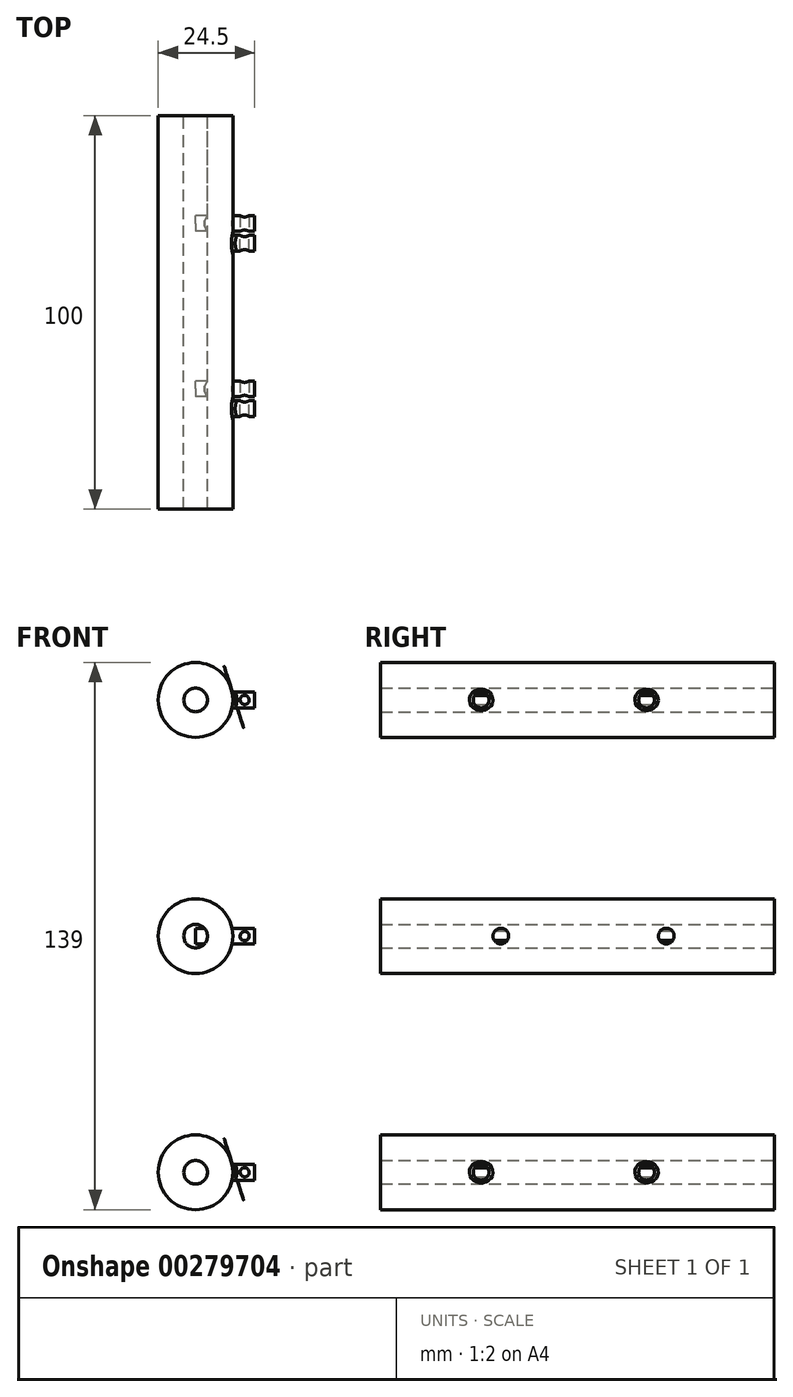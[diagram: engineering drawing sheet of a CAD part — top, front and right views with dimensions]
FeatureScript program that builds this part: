
annotation { "Feature Type Name" : "Feature", "Feature Type Description" : "" }
export const myFeature = defineFeature(function(context is Context, id is Id, definition is map)
    precondition{}
    {
        {
            var Q0;
            Q0=qCreatedBy(makeId("Front.planeOp"),FACE);
            var sketch = newSketch(context, id + "F0", { "sketchPlane" : qUnion([Q0])});
            skCircle(sketch, "E0", {"center": v(0, 0) * mm, "radius": 9.5 * mm});
            skCircle(sketch, "E1", {"center": v(0, 0) * mm, "radius": 3 * mm});
            skSolve(sketch);
        }
        {
            var Q0;
            Q0=makeQuery(id+"F0.imprint","IMPRINT",FACE,{"disambiguationData":[TD([[makeQuery(id+"F0.imprint","IMPRINT",EDGE,{"derivedFrom":sQuery(id+"F0.wireOp",EDGE,"E0")}),1.0]])]});
            extrude(context, id + "F1", {"entities" : qUnion([Q0]), "endBound" : BoundingType.SYMMETRIC, "depth" : 100 * mm});
        }
        {
            var Q0;
            Q0=makeQuery(id+"F1.opExtrude","SWEPT_BODY",BODY,{"disambiguationData":[OSD([sQuery(id+"F0.wireOp",EDGE,"E0"),sQuery(id+"F0.wireOp",EDGE,"E1")])]});
            transform(context, id + "F2", {"entities" : qUnion([Q0]), "transformType" : TransformType.TRANSLATION_3D, "dx" : 0 * mm, "dy" : 0 * mm, "dz" : 60 * mm, "makeCopy" : true});
        }
        {
            var Q0;
            Q0=qCreatedBy(makeId("Right.planeOp"),FACE);
            var sketch = newSketch(context, id + "F3", { "sketchPlane" : qUnion([Q0])});
            skPoint(sketch, "E2", {"position": v(0, 60) * mm});
            skPoint(sketch, "E3", {"position": v(-24.45, 60) * mm});
            skPoint(sketch, "E4", {"position": v(17.57, 60) * mm});
            skCircle(sketch, "E5", {"center": v(17.57, 60) * mm, "radius": 2 * mm});
            skCircle(sketch, "E6", {"center": v(-24.45, 60) * mm, "radius": 2 * mm});
            skSolve(sketch);
        }
        {
            var Q0;
            Q0=makeQuery(id+"F3.imprint","IMPRINT",FACE,{"disambiguationData":[TD([[makeQuery(id+"F3.imprint","IMPRINT",EDGE,{"derivedFrom":sQuery(id+"F3.wireOp",EDGE,"E6")}),1.0]])]});
            var Q1;
            Q1=makeQuery(id+"F3.imprint","IMPRINT",FACE,{"disambiguationData":[TD([[makeQuery(id+"F3.imprint","IMPRINT",EDGE,{"derivedFrom":sQuery(id+"F3.wireOp",EDGE,"E5")}),1.0]])]});
            extrude(context, id + "F4", {"entities" : qUnion([Q0, Q1]), "operationType" : NewBodyOperationType.ADD, "depth" : 15 * mm});
        }
        {
            var Q0;
            Q0=makeQuery(id+"F3.imprint","IMPRINT",FACE,{"disambiguationData":[TD([[makeQuery(id+"F3.imprint","IMPRINT",EDGE,{"derivedFrom":sQuery(id+"F3.wireOp",EDGE,"E6")}),1.0]])]});
            var Q1;
            Q1=makeQuery(id+"F3.imprint","IMPRINT",FACE,{"disambiguationData":[TD([[makeQuery(id+"F3.imprint","IMPRINT",EDGE,{"derivedFrom":sQuery(id+"F3.wireOp",EDGE,"E5")}),1.0]])]});
            var Q2;
            Q2=makeQuery(id+"F2.opPattern","COPY",FACE,{"derivedFrom":makeQuery(id+"F1.opExtrude","SWEPT_FACE",FACE,{"disambiguationData":[OSD([sQuery(id+"F0.wireOp",EDGE,"E1")])]}),"instanceName":"1"});
            extrude(context, id + "F5", {"entities" : qUnion([Q0, Q1]), "operationType" : NewBodyOperationType.REMOVE, "endBound" : BoundingType.UP_TO_SURFACE, "endBoundEntityFace" : qUnion([Q2]), "depth" : 25 * mm});
        }
        {
            var Q0;
            Q0=makeQuery(id+"F4.opExtrude","CAP_FACE",FACE,{"disambiguationData":[OSD([sQuery(id+"F3.wireOp",EDGE,"E6")])],"isStart":false});
            cPlane(context, id + "F6", {"entities" : qUnion([Q0]), "cplaneType" : CPlaneType.OFFSET, "offset" : 2.5 * mm, "oppositeDirection" : true, "width" : 150 * mm, "height" : 150 * mm});
        }
        {
            var Q0;
            Q0=qCreatedBy(makeId("Front.planeOp"),FACE);
            cPlane(context, id + "F7", {"entities" : qUnion([Q0]), "cplaneType" : CPlaneType.OFFSET, "offset" : 18.7 * mm, "width" : 150 * mm, "height" : 150 * mm});
        }
        {
            var Q0;
            Q0=qCreatedBy(id+"F7.planeOp",FACE);
            cPlane(context, id + "F8", {"entities" : qUnion([Q0]), "cplaneType" : CPlaneType.OFFSET, "offset" : 42 * mm, "oppositeDirection" : true, "width" : 150 * mm, "height" : 150 * mm});
        }
        {
            var Q0;
            Q0=qCreatedBy(id+"F8.planeOp",FACE);
            var sketch = newSketch(context, id + "F9", { "sketchPlane" : qUnion([Q0])});
            skPoint(sketch, "E7", {"position": v(12.46, 0) * mm});
            skCircle(sketch, "E8", {"center": v(12.46, 60) * mm, "radius": 1.15 * mm});
            skCircle(sketch, "E9", {"center": v(12.46, 0) * mm, "radius": 1.15 * mm});
            skSolve(sketch);
        }
        {
            var Q0;
            Q0=makeQuery(id+"F9.imprint","IMPRINT",FACE,{"disambiguationData":[TD([[makeQuery(id+"F9.imprint","IMPRINT",EDGE,{"derivedFrom":sQuery(id+"F9.wireOp",EDGE,"E8")}),1.0]])]});
            extrude(context, id + "F10", {"entities" : qUnion([Q0]), "operationType" : NewBodyOperationType.REMOVE, "endBound" : BoundingType.THROUGH_ALL, "depth" : 25 * mm, "hasSecondDirection" : true, "secondDirectionBound" : SecondDirectionBoundingType.THROUGH_ALL, "secondDirectionOppositeDirection" : true, "secondDirectionDepth" : 25 * mm});
        }
        {
            var Q0;
            Q0=makeQuery(id+"F4.boolean.opBoolean","INTERSECT",EDGE,{"derivedFrom":[makeQuery(id+"F2.opPattern","COPY",FACE,{"derivedFrom":makeQuery(id+"F1.opExtrude","SWEPT_FACE",FACE,{"disambiguationData":[OSD([sQuery(id+"F0.wireOp",EDGE,"E0")])]}),"instanceName":"1"}),makeQuery(id+"F4.opExtrude","SWEPT_FACE",FACE,{"disambiguationData":[OSD([sQuery(id+"F3.wireOp",EDGE,"E5")])]})]});
            var Q1;
            Q1=makeQuery(id+"F4.boolean.opBoolean","INTERSECT",EDGE,{"derivedFrom":[makeQuery(id+"F2.opPattern","COPY",FACE,{"derivedFrom":makeQuery(id+"F1.opExtrude","SWEPT_FACE",FACE,{"disambiguationData":[OSD([sQuery(id+"F0.wireOp",EDGE,"E0")])]}),"instanceName":"1"}),makeQuery(id+"F4.opExtrude","SWEPT_FACE",FACE,{"disambiguationData":[OSD([sQuery(id+"F3.wireOp",EDGE,"E6")])]})]});
            fillet(context, id + "F11", {"entities" : qUnion([Q0, Q1]), "radius" : 1 * mm, "tangentPropagation" : true, "rho" : 0.7, "crossSection" : FilletCrossSection.CONIC, "allowEdgeOverflow" : false});
        }
        {
            var Q0;
            Q0=makeQuery(id+"F2.opPattern","COPY",BODY,{"derivedFrom":makeQuery(id+"F1.opExtrude","SWEPT_BODY",BODY,{"disambiguationData":[OSD([sQuery(id+"F0.wireOp",EDGE,"E0"),sQuery(id+"F0.wireOp",EDGE,"E1")])]}),"instanceName":"1"});
            transform(context, id + "F12", {"entities" : qUnion([Q0]), "transformType" : TransformType.TRANSLATION_3D, "dx" : 0 * mm, "dy" : 0 * mm, "dz" : -120 * mm, "makeCopy" : true});
        }
        {
            var Q0;
            Q0=qCreatedBy(makeId("Right.planeOp"),FACE);
            var sketch = newSketch(context, id + "F13", { "sketchPlane" : qUnion([Q0])});
            skPoint(sketch, "E10", {"position": v(0, 0) * mm});
            skPoint(sketch, "E11", {"position": v(-19.45, 0) * mm});
            skPoint(sketch, "E12", {"position": v(22.57, 0) * mm});
            skCircle(sketch, "E13", {"center": v(22.57, 0) * mm, "radius": 2 * mm});
            skCircle(sketch, "E14", {"center": v(-19.45, 0) * mm, "radius": 2 * mm});
            skSolve(sketch);
        }
        {
            var Q0;
            Q0 = qSketchRegion(id + "F13", true);
            extrude(context, id + "F14", {"entities" : qUnion([Q0]), "operationType" : NewBodyOperationType.ADD, "depth" : 15 * mm});
        }
        {
            var Q0;
            Q0=makeQuery(id+"F9.imprint","IMPRINT",FACE,{"disambiguationData":[TD([[makeQuery(id+"F9.imprint","IMPRINT",EDGE,{"derivedFrom":sQuery(id+"F9.wireOp",EDGE,"E9")}),1.0]])]});
            extrude(context, id + "F15", {"entities" : qUnion([Q0]), "operationType" : NewBodyOperationType.REMOVE, "endBound" : BoundingType.THROUGH_ALL, "oppositeDirection" : true, "depth" : 25 * mm, "hasSecondDirection" : true, "secondDirectionBound" : SecondDirectionBoundingType.THROUGH_ALL, "secondDirectionOppositeDirection" : false, "secondDirectionDepth" : 25 * mm});
        }
    });
